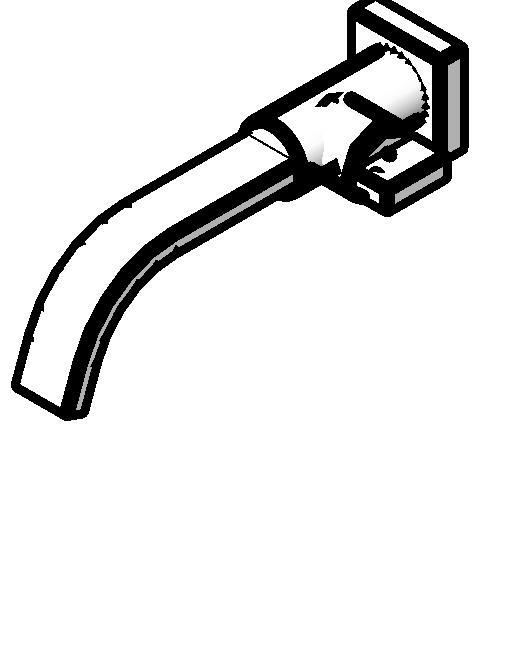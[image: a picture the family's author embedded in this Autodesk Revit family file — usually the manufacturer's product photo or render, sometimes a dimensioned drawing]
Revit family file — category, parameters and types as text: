
# Revit family: Deca_Torneira de parede para lavatório_Polo_1178.33
name_source: partatom
category: Plumbing Fixtures
units: mm (PartAtom-declared; Revit-internal decimal feet)

## family parameters
Cut with Voids When Loaded = No
Host = Face
Part Type = Normal
Room Calculation Point = No
Round Connector Dimension = Use Radius
Shared = No

## types (4) — shared parameters
Acompanha o Produto = Acompanha Deca confort
Aprovado por = quattroD
Atendimento ao Cliente = 0800-0117073
Categoria = METAIS PARA BANHEIRO
Composição Anel Vedação = -
Composição Assento = -
Composição Básica = Liga de Cobre (bronze e latão),Plásticos de Engenharia,Elastômeros
Composição Componente = -
Consumo = -
Cor Interna = -
Cor Secundária = -
Cores Componente = -
Criado por = quattroD
Código Pai = 1178.33
Default Elevation = 1100 mm
Description = Torneira de parede para lavatório
Diâmetro Água Fria = 15 mm
Informações Complementares = -
Itens de Instalação = -
Linha = Polo
Manufacturer = Deca
Norma = NBR10281
Pressão máx. funcionamento = 40 MCA
Pressão mín. Aquec. Acúmulo = -
Pressão mín. Aquec. Passagem = -
Pressão mín. funcionamento = 2 MCA
Raio Água Fria = 7.5 mm  [stored 0.0246063 ft]
Saída de Esgoto = -
Segmento = Banheiro Médio
Tipo de dispositivo economizador = Sim
Tipo de mecanismo utilizado = MVC -1/4 volta
Tipo de rosca de entrada = BSP NBR 8133
Tipo de rosca de saída = -
URL = www.deca.com.br
Vazão na Pressão máx. (L/min) = 6
Vazão na Pressão mín. (L/min) = 4
zero-valued in all types: CWFU

## per-type parameters (varying)
| type | Cor Principal | Material | Model | Peso Líquido (Kg) |
| 1178.C33_Cromado | Cromado | Deca_Cromado | 1178.C33 | 1.05 |
| 1178.BL33.NO_Black Noir | Black Noir | Deca_Black Noir | 1178.BL33.NO | 1.174 |
| 1178.GL33_Gold | Gold | Deca_Gold | 1178.GL33 | 1.174 |
| 1178.GL33.RD_Red Gold | Red Gold | Deca_Red Gold | 1178.GL33.RD | 1.01 |

note: source unit labels omitted for Vazão na Pressão máx. (L/min), Vazão na Pressão mín. (L/min) — the stored unit's dimension contradicts the parameter name (converter mislabeling)

note: [stored X ft] marks values corroborated as IEEE doubles in the binary element streams (Revit-internal decimal feet)

## geometry (parser evidence)
native form markers: Sweep x1
no freeform markers — native parametric forms only
